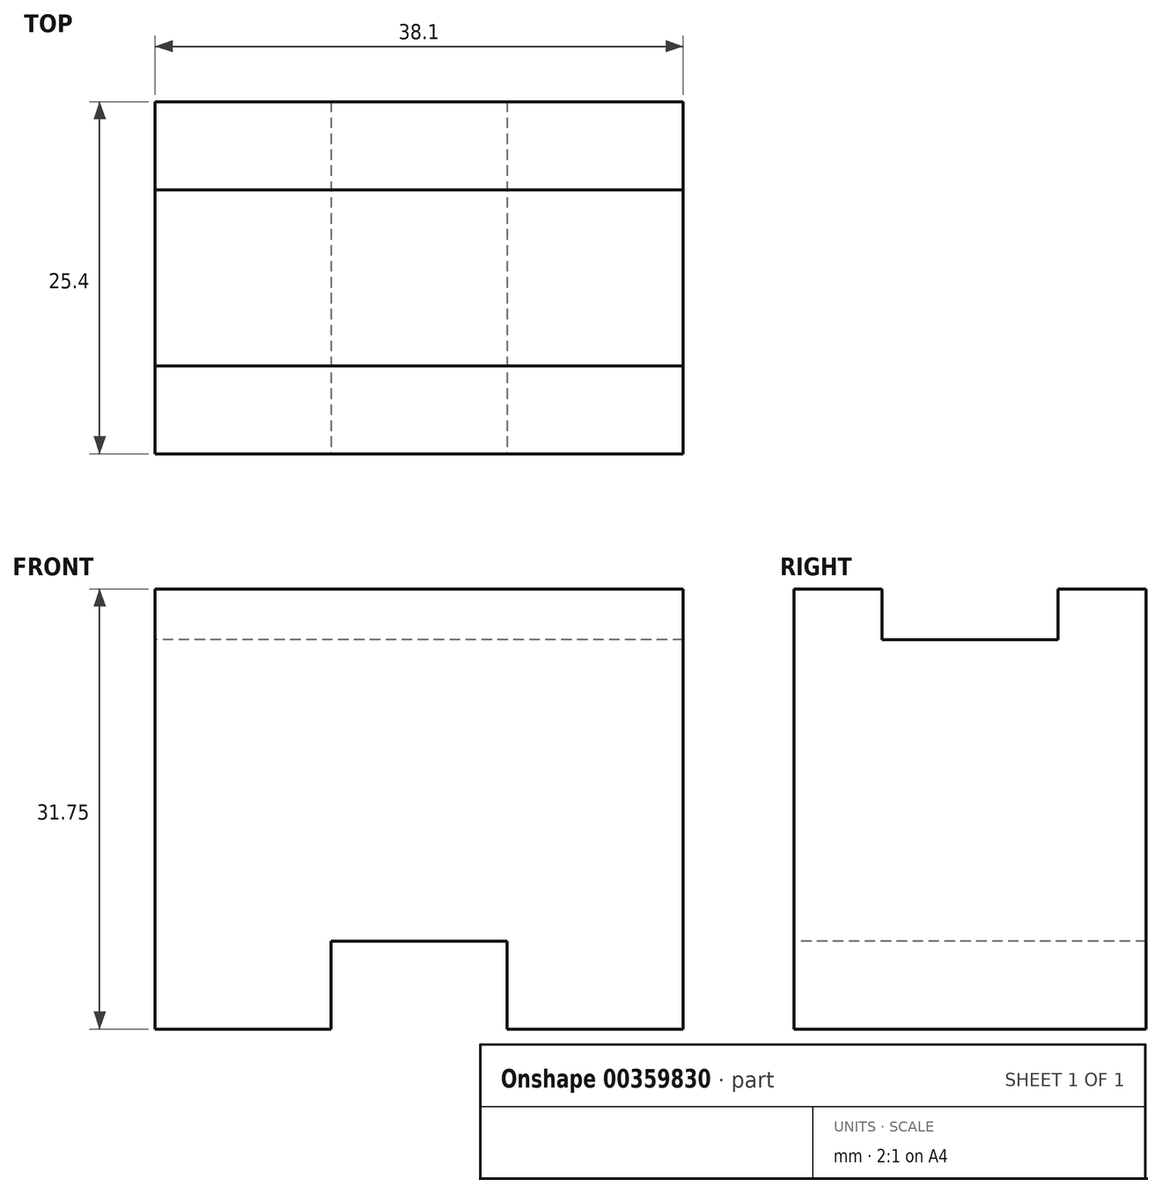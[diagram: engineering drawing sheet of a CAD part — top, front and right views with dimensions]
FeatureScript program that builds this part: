
annotation { "Feature Type Name" : "Feature", "Feature Type Description" : "" }
export const myFeature = defineFeature(function(context is Context, id is Id, definition is map)
    precondition{}
    {
        {
            var Q0;
            Q0=qCreatedBy(makeId("Right.planeOp"),FACE);
            var sketch = newSketch(context, id + "F0", { "sketchPlane" : qUnion([Q0])});
            skLineSegment(sketch, "E0", {"start": v(0, 0) * mm, "end": v(-12.7, 0) * mm});
            skLineSegment(sketch, "E1", {"start": v(-12.7, 0) * mm, "end": v(-12.7, 31.75) * mm});
            skLineSegment(sketch, "E2", {"start": v(-12.7, 31.75) * mm, "end": v(-6.35, 31.75) * mm});
            skLineSegment(sketch, "E3", {"start": v(-6.35, 31.75) * mm, "end": v(-6.35, 28.07) * mm});
            skLineSegment(sketch, "E4", {"start": v(-6.35, 28.07) * mm, "end": v(6.35, 28.07) * mm});
            skLineSegment(sketch, "E5", {"start": v(6.35, 28.07) * mm, "end": v(6.35, 31.75) * mm});
            skLineSegment(sketch, "E6", {"start": v(6.35, 31.75) * mm, "end": v(12.7, 31.75) * mm});
            skLineSegment(sketch, "E7", {"start": v(12.7, 31.75) * mm, "end": v(12.7, 0) * mm});
            skLineSegment(sketch, "E8", {"start": v(12.7, 0) * mm, "end": v(0, 0) * mm});
            skSolve(sketch);
        }
        {
            var Q0;
            Q0 = qSketchRegion(id + "F0", true);
            extrude(context, id + "F1", {"entities" : qUnion([Q0]), "depth" : 38.1 * mm});
        }
        {
            var Q0;
            Q0=qCreatedBy(makeId("Front.planeOp"),FACE);
            var sketch = newSketch(context, id + "F2", { "sketchPlane" : qUnion([Q0])});
            skLineSegment(sketch, "E9", {"start": v(12.7, 0) * mm, "end": v(12.7, 6.35) * mm});
            skLineSegment(sketch, "E10", {"start": v(12.7, 6.35) * mm, "end": v(25.4, 6.35) * mm});
            skLineSegment(sketch, "E11", {"start": v(25.4, 6.35) * mm, "end": v(25.4, 0) * mm});
            skLineSegment(sketch, "E12", {"start": v(25.4, 0) * mm, "end": v(12.7, 0) * mm});
            skSolve(sketch);
        }
        {
            var Q0;
            Q0 = qSketchRegion(id + "F2", true);
            extrude(context, id + "F3", {"entities" : qUnion([Q0]), "operationType" : NewBodyOperationType.REMOVE, "oppositeDirection" : true, "depth" : 25.4 * mm});
        }
        {
            var Q0;
            Q0 = qSketchRegion(id + "F2", true);
            extrude(context, id + "F4", {"entities" : qUnion([Q0]), "operationType" : NewBodyOperationType.REMOVE, "oppositeDirection" : true, "depth" : 50.8 * mm});
        }
        {
            var Q0;
            Q0 = qSketchRegion(id + "F2", true);
            extrude(context, id + "F5", {"entities" : qUnion([Q0]), "operationType" : NewBodyOperationType.REMOVE, "depth" : 25.4 * mm});
        }
    });
